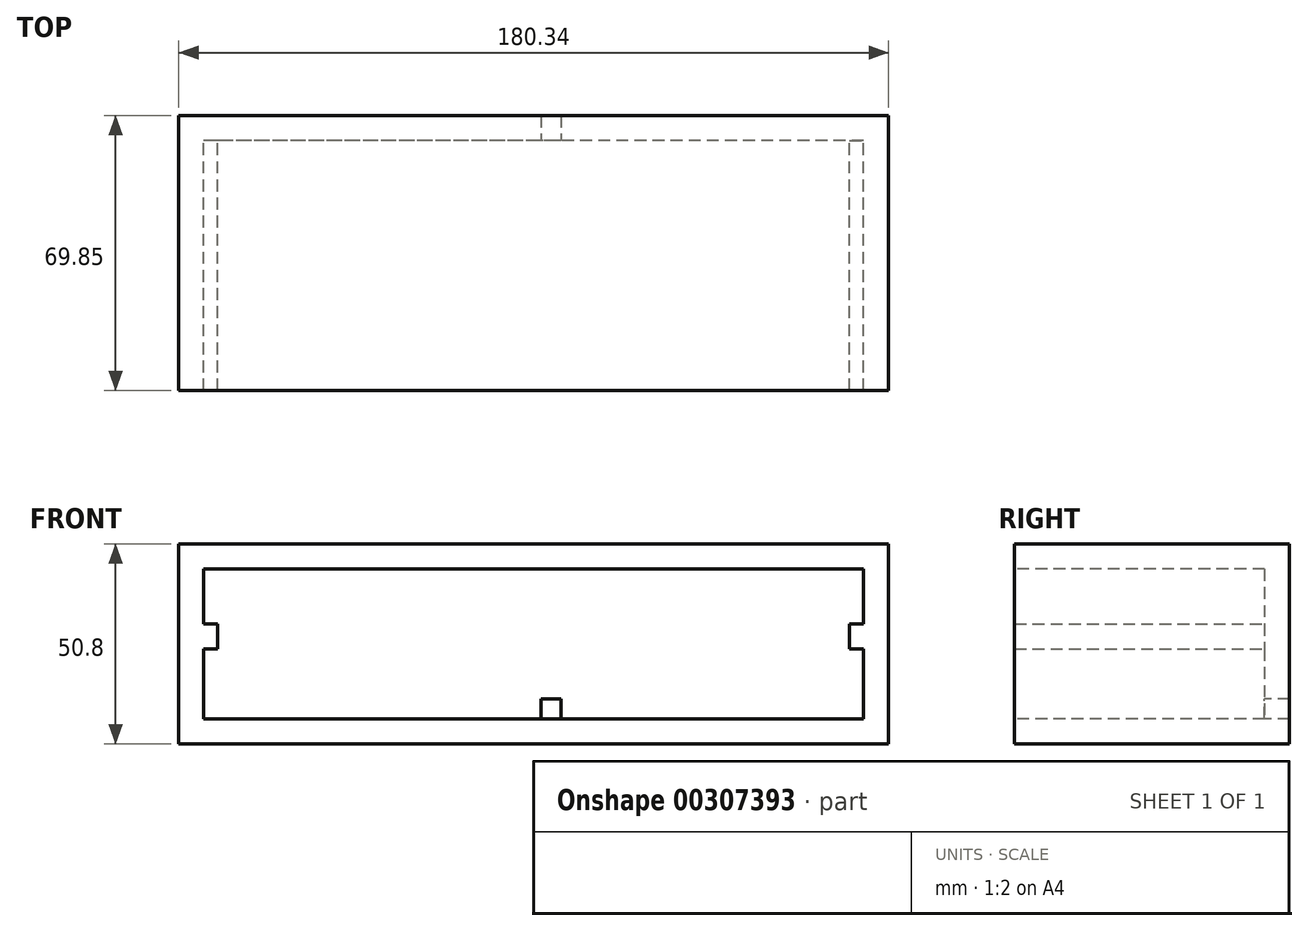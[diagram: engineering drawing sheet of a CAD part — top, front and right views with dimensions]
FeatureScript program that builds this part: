
annotation { "Feature Type Name" : "Feature", "Feature Type Description" : "" }
export const myFeature = defineFeature(function(context is Context, id is Id, definition is map)
    precondition{}
    {
        {
            var Q0;
            Q0=qCreatedBy(makeId("Top.planeOp"),FACE);
            var sketch = newSketch(context, id + "F0", { "sketchPlane" : qUnion([Q0])});
            skLineSegment(sketch, "E0.bottom", {"start": v(83.82, 31.75) * mm, "end": v(-83.82, 31.75) * mm});
            skLineSegment(sketch, "E0.top", {"start": v(83.82, -31.75) * mm, "end": v(-83.82, -31.75) * mm});
            skLineSegment(sketch, "E0.left", {"start": v(83.82, 31.75) * mm, "end": v(83.82, -31.75) * mm});
            skLineSegment(sketch, "E0.right", {"start": v(-83.82, 31.75) * mm, "end": v(-83.82, -31.75) * mm});
            skPoint(sketch, "E0.middle", {"position": v(0, 0) * mm});
            skSolve(sketch);
        }
        {
            var Q0;
            Q0 = qSketchRegion(id + "F0", true);
            extrude(context, id + "F1", {"entities" : qUnion([Q0]), "depth" : 38.1 * mm});
        }
        {
            var Q0;
            Q0=makeQuery(id+"F1.opExtrude","SWEPT_FACE",FACE,{"disambiguationData":[OSD([sQuery(id+"F0.wireOp",EDGE,"E0.top")])]});
            shell(context, id + "F2", {"entities" : qUnion([Q0]), "thickness" : 6.35 * mm, "oppositeDirection" : true});
        }
        {
            var Q0;
            Q0=makeQuery(id+"F2.opShell","OFFSET_FACE",FACE,{"disambiguationData":[OSD([sQuery(id+"F0.wireOp",EDGE,"E0.bottom")])]});
            var sketch = newSketch(context, id + "F3", { "sketchPlane" : qUnion([Q0])});
            skLineSegment(sketch, "E1.bottom", {"start": v(6.99, 0) * mm, "end": v(1.9, 0) * mm});
            skLineSegment(sketch, "E1.top", {"start": v(6.99, 5.08) * mm, "end": v(1.9, 5.08) * mm});
            skLineSegment(sketch, "E1.left", {"start": v(6.99, 0) * mm, "end": v(6.99, 5.08) * mm});
            skLineSegment(sketch, "E1.right", {"start": v(1.9, 0) * mm, "end": v(1.9, 5.08) * mm});
            skPoint(sketch, "E1.middle", {"position": v(0, 2.54) * mm});
            skSolve(sketch);
        }
        {
            var Q0;
            Q0=makeQuery(id+"F3.imprint","IMPRINT",FACE,{"disambiguationData":[TD([[makeQuery(id+"F3.imprint","IMPRINT",EDGE,{"derivedFrom":sQuery(id+"F3.wireOp",EDGE,"E1.bottom")}),-1.0]])]});
            extrude(context, id + "F4", {"entities" : qUnion([Q0]), "operationType" : NewBodyOperationType.REMOVE, "oppositeDirection" : true, "depth" : 6.35 * mm});
        }
        {
            var Q0;
            Q0=makeQuery(id+"F2.opShell","OFFSET_FACE",FACE,{"disambiguationData":[OSD([sQuery(id+"F0.wireOp",EDGE,"E0.right")])]});
            var sketch = newSketch(context, id + "F5", { "sketchPlane" : qUnion([Q0])});
            skLineSegment(sketch, "E2", {"start": v(-31.75, 17.78) * mm, "end": v(31.75, 17.78) * mm});
            skLineSegment(sketch, "E3", {"start": v(-31.75, 24.13) * mm, "end": v(31.75, 24.13) * mm});
            skSolve(sketch);
        }
        {
            var Q0;
            {var subQ0=sQuery(id+"F5.wireOp",EDGE,"E2");Q0=makeQuery(id+"F5.imprint","IMPRINT",FACE,{"disambiguationData":[TD([[makeQuery(id+"F5.imprint","IMPRINT",EDGE,{"derivedFrom":subQ0}),1.0]])]});}
            extrude(context, id + "F6", {"entities" : qUnion([Q0]), "operationType" : NewBodyOperationType.ADD, "depth" : 3.56 * mm});
        }
        {
            var Q0;
            Q0=makeQuery(id+"F2.opShell","OFFSET_FACE",FACE,{"disambiguationData":[OSD([sQuery(id+"F0.wireOp",EDGE,"E0.left")])]});
            var sketch = newSketch(context, id + "F7", { "sketchPlane" : qUnion([Q0])});
            skLineSegment(sketch, "E4", {"start": v(31.75, 17.78) * mm, "end": v(-31.75, 17.78) * mm});
            skLineSegment(sketch, "E5", {"start": v(-31.75, 24.13) * mm, "end": v(31.75, 24.13) * mm});
            skSolve(sketch);
        }
        {
            var Q0;
            {var subQ0=sQuery(id+"F7.wireOp",EDGE,"E4");Q0=makeQuery(id+"F7.imprint","IMPRINT",FACE,{"disambiguationData":[TD([[makeQuery(id+"F7.imprint","IMPRINT",EDGE,{"derivedFrom":subQ0}),-1.0]])]});}
            extrude(context, id + "F8", {"entities" : qUnion([Q0]), "operationType" : NewBodyOperationType.ADD, "depth" : 3.56 * mm});
        }
    });
